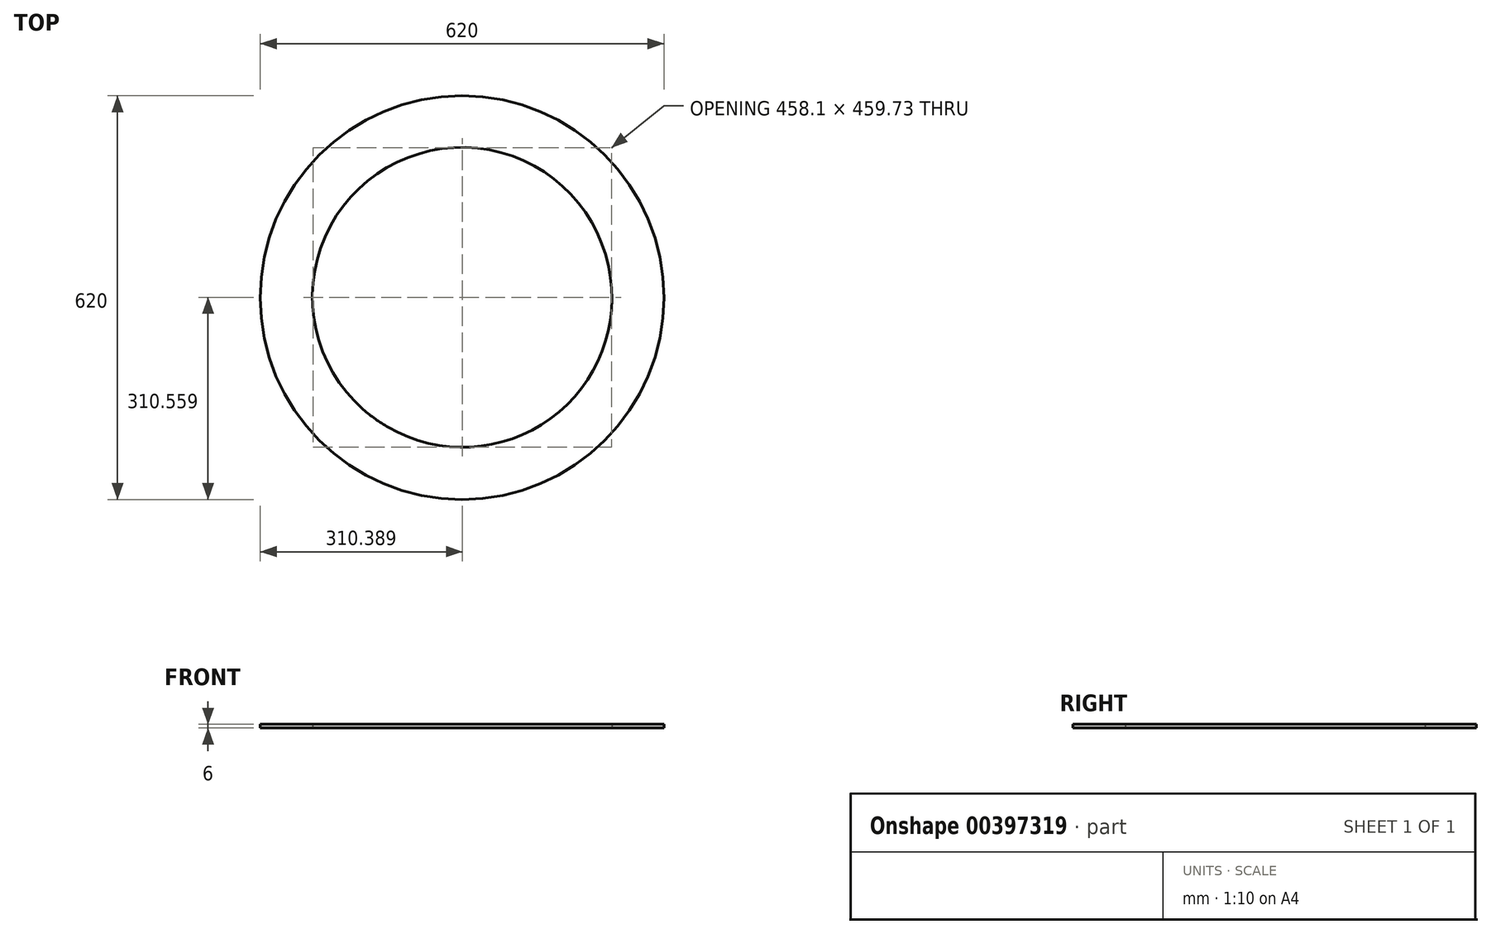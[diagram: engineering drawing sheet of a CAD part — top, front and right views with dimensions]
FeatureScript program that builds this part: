
annotation { "Feature Type Name" : "Feature", "Feature Type Description" : "" }
export const myFeature = defineFeature(function(context is Context, id is Id, definition is map)
    precondition{}
    {
        {
            var Q0;
            Q0=qCreatedBy(makeId("Top.planeOp"),FACE);
            var sketch = newSketch(context, id + "F0", { "sketchPlane" : qUnion([Q0])});
            skCircle(sketch, "E0", {"center": v(0, 0) * mm, "radius": 310 * mm});
            skCircle(sketch, "E1", {"center": v(0, 0) * mm, "radius": 229 * mm});
            skCircle(sketch, "E2.1.5", {"center": v(1.11, -0.64) * mm, "radius": 229 * mm});
            skCircle(sketch, "E2.2.5", {"center": v(0, 1) * mm, "radius": 229.75 * mm});
            skSolve(sketch);
        }
        {
            var Q0;
            Q0 = qSketchRegion(id + "F0", true);
            extrude(context, id + "F1", {"entities" : qUnion([Q0]), "depth" : 6 * mm});
        }
    });
